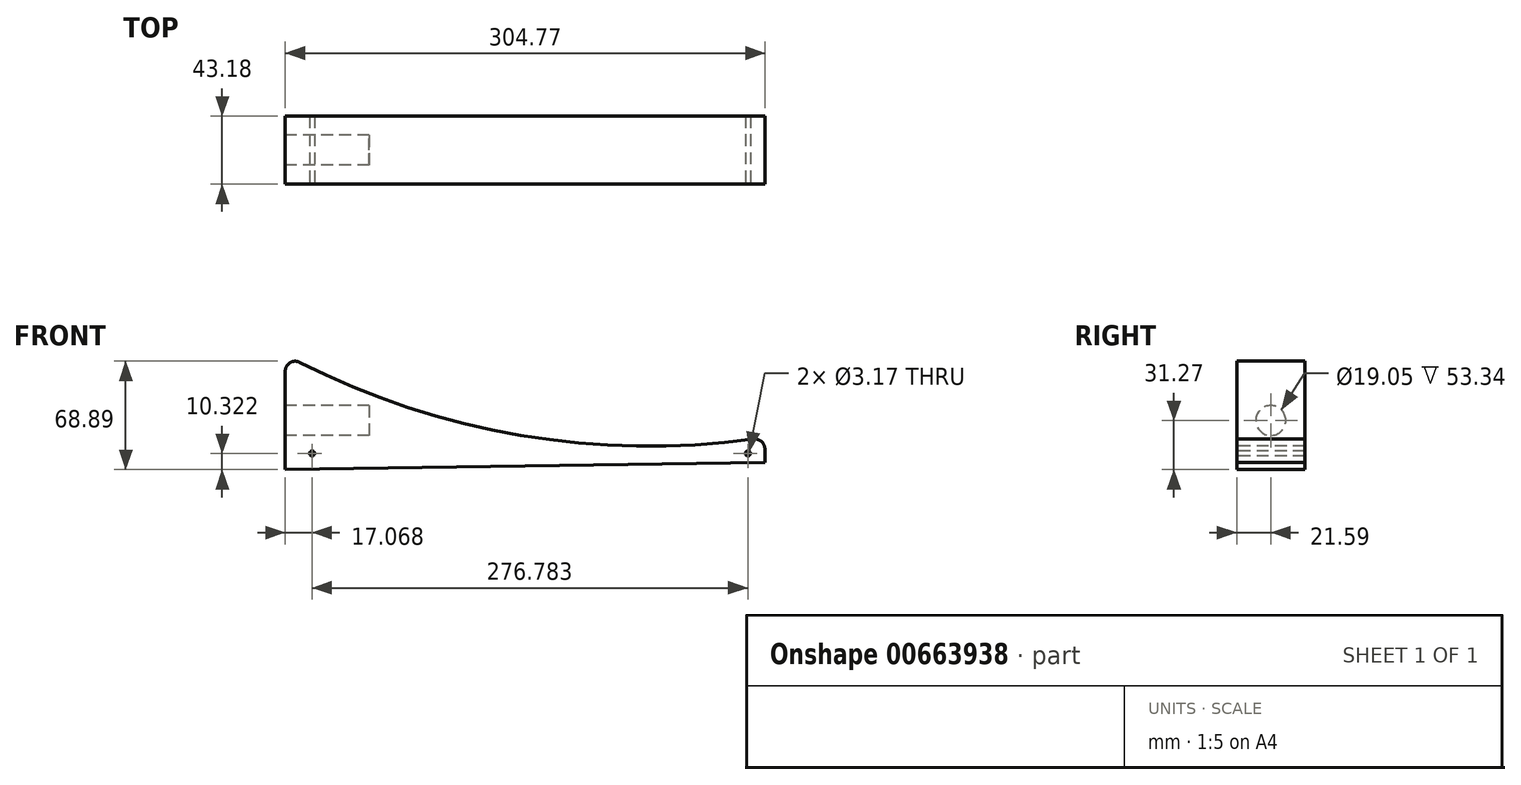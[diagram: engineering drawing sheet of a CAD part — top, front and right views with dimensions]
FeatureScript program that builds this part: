
annotation { "Feature Type Name" : "Feature", "Feature Type Description" : "" }
export const myFeature = defineFeature(function(context is Context, id is Id, definition is map)
    precondition{}
    {
        {
            var Q0;
            Q0=qCreatedBy(makeId("Front.planeOp"),FACE);
            var sketch = newSketch(context, id + "F0", { "sketchPlane" : qUnion([Q0])});
            skLineSegment(sketch, "E0", {"start": v(0, 0) * mm, "end": v(0, 62.54) * mm});
            skLineSegment(sketch, "E1", {"start": v(0, 0) * mm, "end": v(304.77, 4.56) * mm});
            skLineSegment(sketch, "E2", {"start": v(304.77, 4.56) * mm, "end": v(304.64, 13.21) * mm});
            skArc(sketch, "E3", {"start": v(9.23, 68.2) * mm, "mid": v(149.6, 21.77) * mm, "end": v(297.43, 19.4) * mm});
            skPoint(sketch, "E4.visualSharp", {"position": v(304.53, 20.43) * mm});
            skArc(sketch, "E4.filletArc", {"start": v(304.64, 13.21) * mm, "mid": v(302.43, 17.93) * mm, "end": v(297.43, 19.4) * mm});
            skPoint(sketch, "E5.visualSharp", {"position": v(0, 73.03) * mm});
            skArc(sketch, "E5.filletArc", {"start": v(9.23, 68.2) * mm, "mid": v(3.03, 67.95) * mm, "end": v(0, 62.54) * mm});
            skSolve(sketch);
        }
        {
            var Q0;
            Q0=makeQuery(id+"F0.imprint","IMPRINT",FACE,{"disambiguationData":[TD([[makeQuery(id+"F0.imprint","IMPRINT",EDGE,{"derivedFrom":sQuery(id+"F0.wireOp",EDGE,"E0")}),-1.0]])]});
            extrude(context, id + "F1", {"entities" : qUnion([Q0]), "oppositeDirection" : true, "depth" : 43.18 * mm, "offsetDistance" : 25.4 * mm});
        }
        {
            var Q0;
            Q0=makeQuery(id+"F1.opExtrude","CAP_FACE",FACE,{"disambiguationData":[OSD([sQuery(id+"F0.wireOp",EDGE,"E0"),sQuery(id+"F0.wireOp",EDGE,"E1"),sQuery(id+"F0.wireOp",EDGE,"E2"),sQuery(id+"F0.wireOp",EDGE,"bG8aKLgZ-d66L-iBcR-khmt-Ti53vkS9ppNA")])],"isStart":true});
            var sketch = newSketch(context, id + "F2", { "sketchPlane" : qUnion([Q0])});
            skSolve(sketch);
        }
        {
            var Q0;
            Q0=makeQuery(id+"F1.opExtrude","SWEPT_FACE",FACE,{"disambiguationData":[OSD([sQuery(id+"F0.wireOp",EDGE,"E0")])]});
            var sketch = newSketch(context, id + "F3", { "sketchPlane" : qUnion([Q0])});
            skCircle(sketch, "E6", {"center": v(-21.59, 31.27) * mm, "radius": 9.53 * mm});
            skPoint(sketch, "E6.centerSnap0", {"position": v(0, 31.27) * mm});
            skPoint(sketch, "E6.centerSnap1", {"position": v(-21.59, 0) * mm});
            skSolve(sketch);
        }
        {
            var Q0;
            Q0=makeQuery(id+"F3.imprint","IMPRINT",FACE,{"disambiguationData":[TD([[makeQuery(id+"F3.imprint","IMPRINT",EDGE,{"derivedFrom":sQuery(id+"F3.wireOp",EDGE,"E6")}),1.0]])]});
            extrude(context, id + "F4", {"entities" : qUnion([Q0]), "operationType" : NewBodyOperationType.REMOVE, "oppositeDirection" : true, "depth" : 53.34 * mm, "offsetDistance" : 25.4 * mm});
        }
        {
            var Q0;
            Q0=makeQuery(id+"F2.imprint","IMPRINT",FACE,{"disambiguationData":[TD([[makeQuery(id+"F2.imprint","IMPRINT",EDGE,{"derivedFrom":makeQuery(id+"F1.opExtrude","CAP_EDGE",EDGE,{"disambiguationData":[OSD([sQuery(id+"F0.wireOp",EDGE,"E0")])],"isStart":true})}),-1.0]])]});
            var sketch = newSketch(context, id + "F5", { "sketchPlane" : qUnion([Q0])});
            skCircle(sketch, "E7", {"center": v(293.85, 10.32) * mm, "radius": 1.59 * mm});
            skCircle(sketch, "E8", {"center": v(17.07, 10.32) * mm, "radius": 1.59 * mm});
            skSolve(sketch);
        }
        {
            var Q0;
            Q0=makeQuery(id+"F5.imprint","IMPRINT",FACE,{"disambiguationData":[TD([[makeQuery(id+"F5.imprint","IMPRINT",EDGE,{"derivedFrom":sQuery(id+"F5.wireOp",EDGE,"E8")}),1.0]])]});
            var Q1;
            Q1=makeQuery(id+"F5.imprint","IMPRINT",FACE,{"disambiguationData":[TD([[makeQuery(id+"F5.imprint","IMPRINT",EDGE,{"derivedFrom":sQuery(id+"F5.wireOp",EDGE,"E7")}),1.0]])]});
            extrude(context, id + "F6", {"entities" : qUnion([Q0, Q1]), "operationType" : NewBodyOperationType.REMOVE, "oppositeDirection" : true, "depth" : 57.15 * mm, "offsetDistance" : 25.4 * mm});
        }
    });
